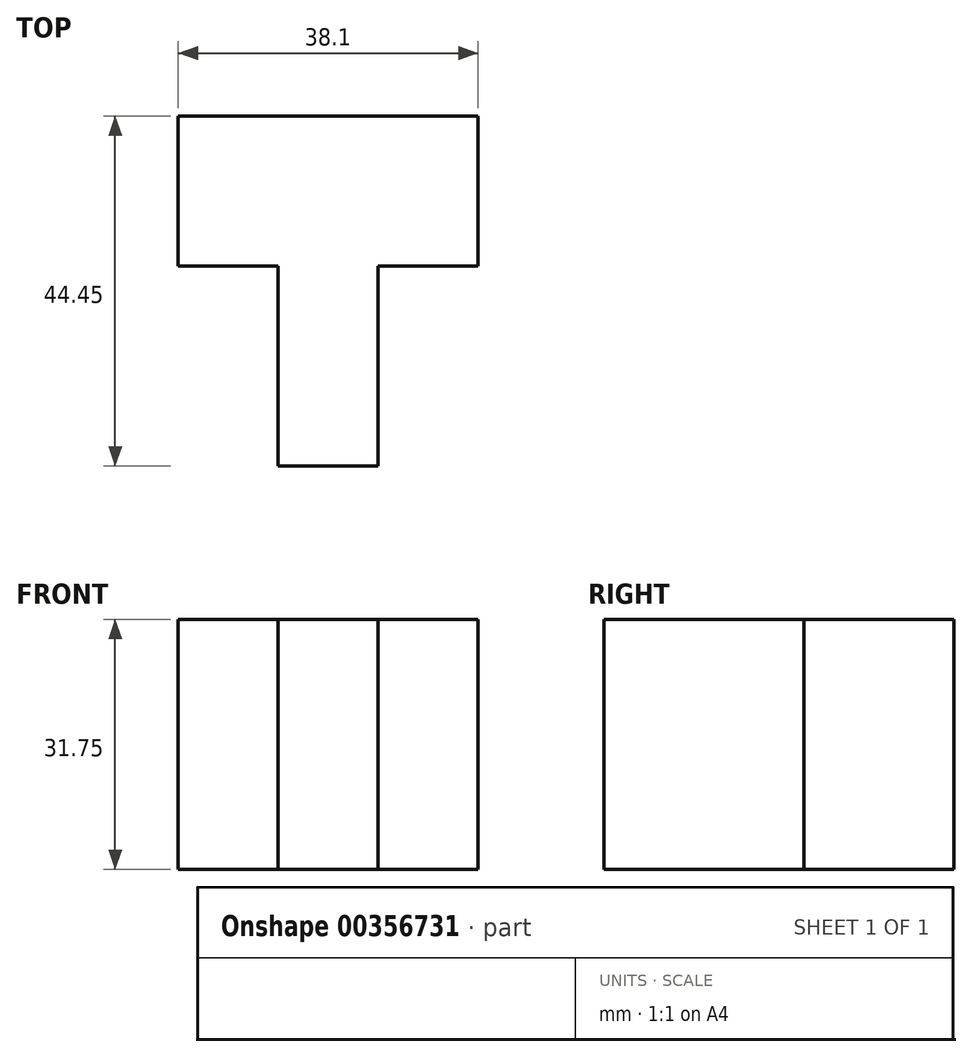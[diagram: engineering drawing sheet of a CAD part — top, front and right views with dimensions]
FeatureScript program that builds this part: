
annotation { "Feature Type Name" : "Feature", "Feature Type Description" : "" }
export const myFeature = defineFeature(function(context is Context, id is Id, definition is map)
    precondition{}
    {
        {
            var Q0;
            Q0=qCreatedBy(makeId("Top.planeOp"),FACE);
            var sketch = newSketch(context, id + "F0", { "sketchPlane" : qUnion([Q0])});
            skLineSegment(sketch, "E0", {"start": v(-56.88, 44.45) * mm, "end": v(-18.78, 44.45) * mm});
            skLineSegment(sketch, "E1", {"start": v(-18.78, 44.45) * mm, "end": v(-18.78, 25.4) * mm});
            skLineSegment(sketch, "E2", {"start": v(-18.78, 25.4) * mm, "end": v(-31.48, 25.4) * mm});
            skLineSegment(sketch, "E3", {"start": v(-31.48, 25.4) * mm, "end": v(-31.48, 0) * mm});
            skLineSegment(sketch, "E4", {"start": v(-31.48, 0) * mm, "end": v(-44.18, 0) * mm});
            skLineSegment(sketch, "E5", {"start": v(-44.18, 0) * mm, "end": v(-44.18, 25.4) * mm});
            skLineSegment(sketch, "E6", {"start": v(-44.18, 25.4) * mm, "end": v(-56.88, 25.4) * mm});
            skLineSegment(sketch, "E7", {"start": v(-56.88, 25.4) * mm, "end": v(-56.88, 44.45) * mm});
            skSolve(sketch);
        }
        {
            var Q0;
            Q0 = qSketchRegion(id + "F0", true);
            extrude(context, id + "F1", {"entities" : qUnion([Q0]), "depth" : 31.75 * mm});
        }
    });
